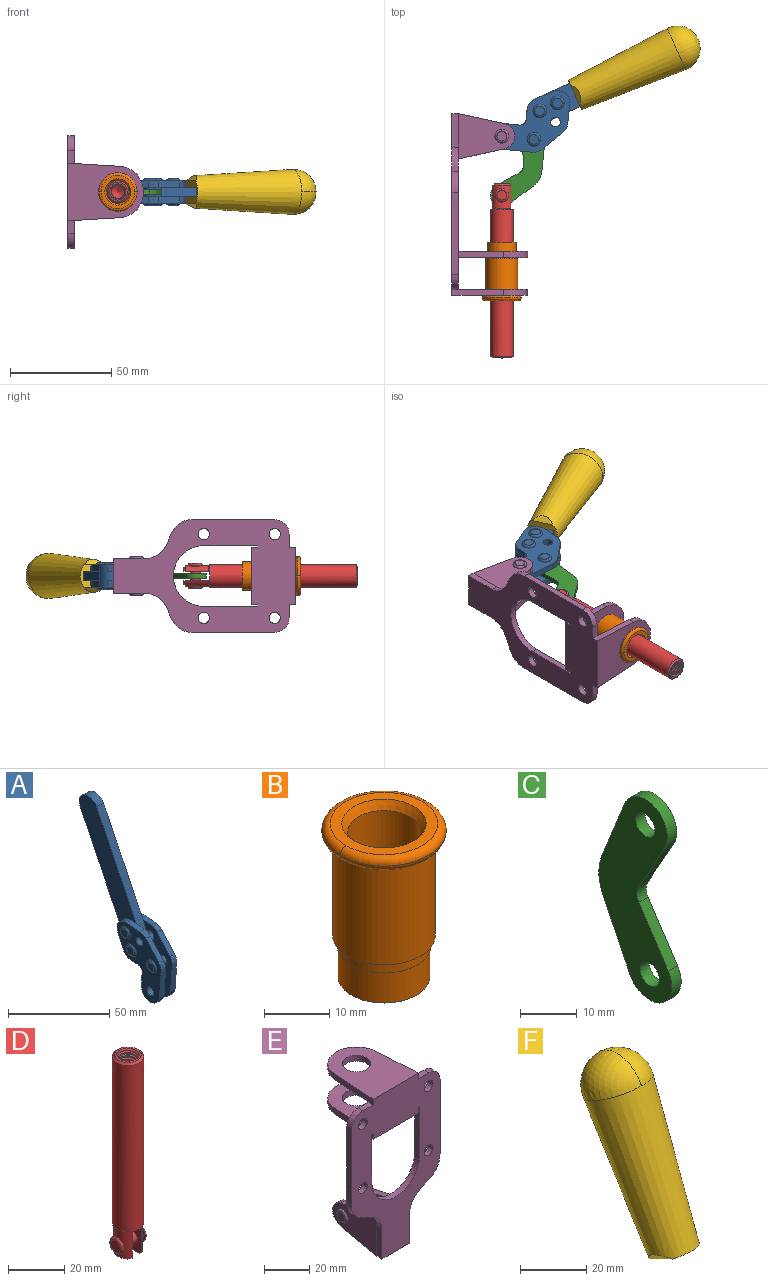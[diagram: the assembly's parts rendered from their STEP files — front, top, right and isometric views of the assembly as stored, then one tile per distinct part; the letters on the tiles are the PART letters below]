
ASSEMBLY  parts=6 mates=6
PART A: 59 faces, bbox 12.9x60.2x99.6 mm
  f0: torus R=2.39mm, axis (-1,0,0), area 14.9mm2, adj f20,f43,f51
  f1: torus R=2.39mm, axis (-1,0,0), area 14.9mm2, adj f19,f42,f51
  f2: torus R=2.39mm, axis (-1,0,0), area 14.9mm2, adj f18,f35,f51
  f3: torus R=2.39mm, axis (-1,0,0), area 14.9mm2, adj f14,f17,f23
  f4: torus R=2.39mm, axis (-1,0,0), area 14.9mm2, adj f13,f16,f23
  f5: torus R=2.39mm, axis (-1,0,0), area 14.9mm2, adj f12,f15,f23
  f6: cylinder r=2.39mm len=4.78mm, axis (1,0,0), area 46.5mm2, adj f48,f50,f51
  f7: cylinder r=2.39mm len=4.78mm, axis (1,0,0), area 46.5mm2, adj f50,f51
  f8: cylinder r=6.35mm len=12.68mm, axis (1,0,0), area 61.8mm2, adj f38,f39,f50,f51
  f9: cylinder r=2.39mm len=4.78mm, axis (-1,0,0), area 70.5mm2, adj f46,f50
  f10: cylinder r=2.39mm len=4.78mm, axis (-1,0,0), area 46.5mm2, adj f23,f45,f46
  f11: cylinder r=2.39mm len=4.78mm, axis (-1,0,0), area 46.5mm2, adj f23,f46
  f12: plane 4.78x4.78mm, normal (1,0,0), area 17.9mm2, adj f5,f15
  f13: plane 4.78x4.78mm, normal (1,0,0), area 17.9mm2, adj f4,f16
  f14: plane 4.78x4.78mm, normal (1,0,0), area 17.9mm2, adj f3,f17
  f15: torus R=2.39mm, axis (-1,0,0), area 14.9mm2, adj f5,f12,f23
  f16: torus R=2.39mm, axis (-1,0,0), area 14.9mm2, adj f4,f13,f23
  f17: torus R=2.39mm, axis (-1,0,0), area 14.9mm2, adj f3,f14,f23
  f18: plane 4.78x4.78mm, normal (-1,0,0), area 17.9mm2, adj f2,f35
  f19: plane 4.78x4.78mm, normal (-1,0,0), area 17.9mm2, adj f1,f42
  f20: plane 4.78x4.78mm, normal (-1,0,0), area 17.9mm2, adj f0,f43
  f21: plane 2.26x0.2mm, normal (1,0,0), area 0.2mm2, adj f31,f44
  f22: plane 2.26x0.2mm, normal (-1,0,0), area 0.2mm2, adj f41,f44
  f23: plane 39.37x30.77mm, normal (1,0,0), area 565.5mm2, adj f3,f4,f5,f10,f11,f15,f16,f17
  f24: cylinder r=6.1mm len=4.15mm, axis (-1,0,0), area 14.7mm2, adj f23,f25,f32,f46
  f25: plane 10.25x9.01mm, normal (0,-0.75,0.66), area 42.3mm2, adj f23,f24,f26,f46
  f26: cylinder r=6.35mm len=4.64mm, axis (-1,0,0), area 15.6mm2, adj f23,f25,f27,f46
  f27: plane 15.84x3.1mm, normal (0,-1,-0.07), area 49.2mm2, adj f23,f26,f28,f46
  f28: cylinder r=6.35mm len=12.68mm, axis (-1,0,0), area 61.8mm2, adj f23,f27,f29,f46
  f29: plane 8.11x3.1mm, normal (0,1,0.07), area 25.2mm2, adj f23,f28,f30,f46
  f30: cylinder r=3.05mm len=3.25mm, axis (-1,0,0), area 14.8mm2, adj f23,f29,f31,f46
  f31: plane 5.99x3.1mm, normal (0,0.07,-1), area 18.6mm2, adj f21,f23,f30,f44,f46
  f32: plane 9.5x3.1mm, normal (0,-0.07,1), area 29.5mm2, adj f23,f24,f33,f46,f47
  f33: cylinder r=6.1mm len=8.63mm, axis (-1,0,0), area 39.1mm2, adj f23,f32,f34,f47
  f34: plane 8.65x3.96mm, normal (0,0.91,-0.42), area 29.5mm2, adj f23,f33,f44,f47
  f35: torus R=2.39mm, axis (-1,0,0), area 14.9mm2, adj f2,f18,f51
  f36: plane 10.25x9.01mm, normal (0,-0.75,0.66), area 42.3mm2, adj f37,f49,f50,f51
  f37: cylinder r=6.35mm len=4.64mm, axis (1,0,0), area 15.6mm2, adj f36,f38,f50,f51
  f38: plane 15.84x3.1mm, normal (0,-1,-0.07), area 49.2mm2, adj f8,f37,f50,f51
  f39: plane 8.11x3.1mm, normal (0,1,0.07), area 25.2mm2, adj f8,f40,f50,f51
  f40: cylinder r=3.05mm len=3.25mm, axis (1,0,0), area 14.8mm2, adj f39,f41,f50,f51
  f41: plane 5.99x3.1mm, normal (0,0.07,-1), area 18.6mm2, adj f22,f40,f44,f50,f51
  f42: torus R=2.39mm, axis (-1,0,0), area 14.9mm2, adj f1,f19,f51
  f43: torus R=2.39mm, axis (-1,0,0), area 14.9mm2, adj f0,f20,f51
  f44: cylinder r=6.35mm len=12.12mm, axis (-1,0,0), area 128.9mm2, adj f21,f22,f23,f31,f34,f41,f46,f47
  f45: plane 2.65x1.35mm, normal (1,0,0), area 1mm2, adj f10,f55
  f46: plane 39.08x20.42mm, normal (-1,0,0), area 412.5mm2, adj f9,f10,f11,f24,f25,f26,f27,f28
  f47: plane 77.62x39.82mm, normal (1,0,0), area 850mm2, adj f32,f33,f34,f44,f53,f54,f55
  f48: plane 2.65x1.35mm, normal (-1,0,0), area 1mm2, adj f6,f55
  f49: cylinder r=6.1mm len=4.15mm, axis (1,0,0), area 14.7mm2, adj f36,f50,f51,f56
  f50: plane 39.08x20.42mm, normal (1,0,0), area 412.5mm2, adj f6,f7,f8,f9,f36,f37,f38,f39
  f51: plane 39.37x30.77mm, normal (-1,0,0), area 565.5mm2, adj f0,f1,f2,f6,f7,f8,f35,f36
  f52: plane 8.65x3.96mm, normal (0,0.91,-0.42), area 29.5mm2, adj f44,f51,f57,f58
  f53: plane 68.49x33.4mm, normal (0,0.9,-0.44), area 358.1mm2, adj f44,f47,f54,f58
  f54: cylinder r=6.35mm len=12.06mm, axis (1,0,0), area 93.7mm2, adj f47,f53,f55,f58
  f55: plane 68.49x33.4mm, normal (0,-0.9,0.44), area 358.1mm2, adj f44,f45,f46,f47,f48,f50,f54,f58
  f56: plane 9.5x3.1mm, normal (0,-0.07,1), area 29.5mm2, adj f49,f50,f51,f57,f58
  f57: cylinder r=6.1mm len=8.63mm, axis (1,0,0), area 39.1mm2, adj f51,f52,f56,f58
  f58: plane 77.62x39.82mm, normal (-1,0,0), area 850mm2, adj f44,f52,f53,f54,f55,f56,f57
PART B: 15 faces, bbox 20.6x20.6x28.7 mm
  f0: torus R=8.26mm, axis (0,0,1), area 56.8mm2, adj f1,f10,f12
  f1: torus R=8.26mm, axis (0,0,1), area 56.8mm2, adj f0,f6,f13
  f2: cylinder r=5.59mm len=25.91mm, axis (0,0,1), area 909.6mm2, adj f3,f4
  f3: cone r=6.86mm half-angle=45deg, axis (0,0,-1), area 70.2mm2, adj f2,f14
  f4: cone r=6.47mm half-angle=30deg, axis (0,0,1), area 66.7mm2, adj f2,f13
  f5: cylinder r=7.04mm len=14.07mm, axis (0,0,1), area 252.6mm2, adj f11,f14
  f6: torus R=8.26mm, axis (0,0,1), area 56.8mm2, adj f1,f12,f13
  f7: cylinder r=7.16mm len=14.33mm, axis (0,0,1), area 91.5mm2, adj f9,f11
  f8: cylinder r=7.86mm len=18.42mm, axis (0,0,1), area 909.6mm2, adj f9,f10
  f9: plane 15.72x15.72mm, normal (0,0,-1), area 33mm2, adj f7,f8
  f10: plane 16.51x16.51mm, normal (0,0,-1), area 19.9mm2, adj f0,f8,f12
  f11: plane 14.33x14.33mm, normal (0,0,-1), area 5.7mm2, adj f5,f7
  f12: torus R=8.26mm, axis (0,0,1), area 56.8mm2, adj f0,f6,f10
  f13: plane 16.51x16.51mm, normal (0,0,1), area 82.7mm2, adj f1,f4,f6
  f14: plane 14.07x14.07mm, normal (0,0,-1), area 7.8mm2, adj f3,f5
PART C: 12 faces, bbox 2.3x18.2x42.8 mm
  f0: cylinder r=2.4mm len=4.8mm, axis (1,0,0), area 34.9mm2, adj f4,f11
  f1: cylinder r=10.41mm len=8.47mm, axis (1,0,0), area 20.2mm2, adj f4,f9,f10,f11
  f2: cylinder r=3.05mm len=3.16mm, axis (1,0,0), area 7.7mm2, adj f4,f6,f7,f11
  f3: cylinder r=2.4mm len=4.8mm, axis (1,0,0), area 34.9mm2, adj f4,f11
  f4: plane 42.81x18.23mm, normal (-1,0,0), area 414.1mm2, adj f0,f1,f2,f3,f5,f6,f7,f8
  f5: cylinder r=5.54mm len=10.67mm, axis (1,0,0), area 41.8mm2, adj f4,f6,f10,f11
  f6: plane 11.66x6.53mm, normal (0,-0.87,-0.49), area 30.9mm2, adj f2,f4,f5,f11
  f7: plane 11.17x7.33mm, normal (0,-0.84,0.55), area 30.9mm2, adj f2,f4,f8,f11
  f8: cylinder r=5.54mm len=10.51mm, axis (1,0,0), area 41.8mm2, adj f4,f7,f9,f11
  f9: plane 13.67x6.67mm, normal (0,0.9,-0.44), area 35.1mm2, adj f1,f4,f8,f11
  f10: plane 14.1x5.7mm, normal (0,0.93,0.37), area 35.1mm2, adj f1,f4,f5,f11
  f11: plane 42.81x18.23mm, normal (1,0,0), area 414.1mm2, adj f0,f1,f2,f3,f5,f6,f7,f8
PART D: 48 faces, bbox 12.6x11.1x86.1 mm
  f0: torus R=2.41mm, axis (-1,0,0), area 15mm2, adj f30,f32,f34
  f1: torus R=2.41mm, axis (-1,0,0), area 15mm2, adj f29,f31,f33
  f2: cylinder r=5.54mm len=72.39mm, axis (0,0,1), area 2518.5mm2, adj f3,f4,f42,f43
  f3: cone r=5.54mm half-angle=45deg, axis (0,0,1), area 7.6mm2, adj f2,f5,f41
  f4: cone r=5.54mm half-angle=45deg, axis (0,0,-1), area 34.9mm2, adj f2,f39
  f5: cylinder r=5.08mm len=11.48mm, axis (0,0,1), area 108.3mm2, adj f3,f7,f8,f41
  f6: cylinder r=2.41mm len=4.83mm, axis (-1,0,0), area 71.2mm2, adj f40,f41
  f7: cylinder r=2.41mm len=4.83mm, axis (-1,0,0), area 7.6mm2, adj f5,f34
  f8: cone r=5.08mm half-angle=45deg, axis (0,0,1), area 10.6mm2, adj f5,f37,f41
  f9: cone r=3.98mm half-angle=45deg, axis (0,0,1), area 17.6mm2, adj f27,f39,f45,f46,f47
  f10: cylinder r=2.41mm len=4.83mm, axis (-1,0,0), area 7.6mm2, adj f33,f38
  f11: cylinder r=3.2mm len=6.4mm, axis (0,0,1), area 78.4mm2, adj f12,f28,f44,f45,f47
  f12: cylinder r=3.2mm len=6.4mm, axis (0,0,1), area 10.5mm2, adj f11,f13,f45,f47
  f13: cylinder r=3.2mm len=6.4mm, axis (0,0,1), area 10.5mm2, adj f12,f14,f45,f47
  f14: cylinder r=3.2mm len=6.4mm, axis (0,0,1), area 10.5mm2, adj f13,f15,f45,f47
  f15: cylinder r=3.2mm len=6.4mm, axis (0,0,1), area 10.5mm2, adj f14,f16,f45,f47
  f16: cylinder r=3.2mm len=6.4mm, axis (0,0,1), area 10.5mm2, adj f15,f17,f45,f47
  f17: cylinder r=3.2mm len=6.4mm, axis (0,0,1), area 10.5mm2, adj f16,f18,f45,f47
  f18: cylinder r=3.2mm len=6.4mm, axis (0,0,1), area 10.5mm2, adj f17,f19,f45,f47
  f19: cylinder r=3.2mm len=6.4mm, axis (0,0,1), area 10.5mm2, adj f18,f20,f45,f47
  f20: cylinder r=3.2mm len=6.4mm, axis (0,0,1), area 10.5mm2, adj f19,f21,f45,f47
  f21: cylinder r=3.2mm len=6.4mm, axis (0,0,1), area 10.5mm2, adj f20,f22,f45,f47
  f22: cylinder r=3.2mm len=6.4mm, axis (0,0,1), area 10.5mm2, adj f21,f23,f45,f47
  f23: cylinder r=3.2mm len=6.4mm, axis (0,0,1), area 10.5mm2, adj f22,f24,f45,f47
  f24: cylinder r=3.2mm len=6.4mm, axis (0,0,1), area 10.5mm2, adj f23,f25,f45,f47
  f25: cylinder r=3.2mm len=6.4mm, axis (0,0,1), area 10.5mm2, adj f24,f26,f45,f47
  f26: cylinder r=3.2mm len=6.4mm, axis (0,0,1), area 10.5mm2, adj f25,f27,f45,f47
  f27: cylinder r=3.2mm len=6.4mm, axis (0,0,1), area 7.4mm2, adj f9,f26,f45,f47
  f28: cone r=3.2mm half-angle=60deg, axis (0,0,1), area 37.2mm2, adj f11
  f29: plane 4.83x4.83mm, normal (-1,0,0), area 18.3mm2, adj f1,f31
  f30: plane 4.83x4.83mm, normal (1,0,0), area 18.3mm2, adj f0,f32
  f31: torus R=2.41mm, axis (-1,0,0), area 15mm2, adj f1,f29,f33
  f32: torus R=2.41mm, axis (-1,0,0), area 15mm2, adj f0,f30,f34
  f33: plane 6.83x6.83mm, normal (1,0,0), area 18.3mm2, adj f1,f10,f31
  f34: plane 6.83x6.83mm, normal (-1,0,0), area 18.3mm2, adj f0,f7,f32
  f35: cone r=5.08mm half-angle=45deg, axis (0,0,1), area 10.6mm2, adj f36,f38,f40
  f36: plane 7.25x1.97mm, normal (0,0,-1), area 10mm2, adj f35,f40
  f37: plane 7.25x1.97mm, normal (0,0,-1), area 10mm2, adj f8,f41
  f38: cylinder r=5.08mm len=11.48mm, axis (0,0,1), area 108.3mm2, adj f10,f35,f40,f42
  f39: plane 9.55x9.55mm, normal (0,0,1), area 22mm2, adj f4,f9
  f40: plane 12.76x10.09mm, normal (1,0,0), area 95.7mm2, adj f6,f35,f36,f38,f42,f43
  f41: plane 12.76x10.09mm, normal (-1,0,0), area 95.7mm2, adj f3,f5,f6,f8,f37,f43
  f42: cone r=5.54mm half-angle=45deg, axis (0,0,1), area 7.6mm2, adj f2,f38,f40
  f43: plane 11.07x4.7mm, normal (0,0,-1), area 50.4mm2, adj f2,f40,f41
  f44: plane 0.89x0.62mm, normal (-1,0,0), area 0.3mm2, adj f11,f45,f46,f47
  f45: bspline ~24.8x7.63mm, area 266.6mm2, adj f9,f11,f12,f13,f14,f15,f16,f17
  f46: bspline ~24.87x7.63mm, area 73.6mm2, adj f9,f44,f45,f47
  f47: bspline ~24.98x7.63mm, area 272.5mm2, adj f9,f11,f12,f13,f14,f15,f16,f17
PART E: 55 faces, bbox 55.7x37.4x89.8 mm
  f0: torus R=2.41mm, axis (-1,0,0), area 15mm2, adj f11,f15,f25
  f1: torus R=2.41mm, axis (-1,0,0), area 15mm2, adj f10,f12,f22
  f2: cylinder r=2.78mm len=5.56mm, axis (0,-1,0), area 54.2mm2, adj f30,f54
  f3: cylinder r=14.99mm len=29.97mm, axis (0,-1,0), area 145.9mm2, adj f30,f49,f53,f54
  f4: cylinder r=2.78mm len=5.56mm, axis (0,-1,0), area 54.2mm2, adj f30,f54
  f5: cylinder r=2.78mm len=5.56mm, axis (0,-1,0), area 54.2mm2, adj f30,f54
  f6: cylinder r=2.78mm len=5.56mm, axis (0,-1,0), area 54.2mm2, adj f30,f54
  f7: cylinder r=6.35mm len=12.7mm, axis (0,0,1), area 123.6mm2, adj f27,f51
  f8: cylinder r=6.35mm len=12.7mm, axis (0,0,-1), area 124.7mm2, adj f21,f35
  f9: cylinder r=2.41mm len=11.18mm, axis (-1,0,0), area 169.4mm2, adj f16,f19
  f10: plane 4.83x4.83mm, normal (1,0,0), area 18.3mm2, adj f1,f12
  f11: plane 4.83x4.83mm, normal (-1,0,0), area 18.3mm2, adj f0,f15
  f12: torus R=2.41mm, axis (-1,0,0), area 15mm2, adj f1,f10,f22
  f13: cylinder r=6.35mm len=12.41mm, axis (1,0,0), area 53.4mm2, adj f18,f19,f22,f23
  f14: cylinder r=6.35mm len=12.41mm, axis (-1,0,0), area 53.4mm2, adj f16,f17,f24,f25
  f15: torus R=2.41mm, axis (-1,0,0), area 15mm2, adj f0,f11,f25
  f16: plane 27.86x22.35mm, normal (1,0,0), area 425.4mm2, adj f9,f14,f17,f24,f30
  f17: plane 22.86x4.97mm, normal (0,0.21,0.98), area 72.5mm2, adj f14,f16,f25,f30
  f18: plane 22.86x4.97mm, normal (0,0.21,0.98), area 72.5mm2, adj f13,f19,f22,f30
  f19: plane 27.86x22.35mm, normal (-1,0,0), area 425.4mm2, adj f9,f13,f18,f23,f30
  f20: cylinder r=12.7mm len=25.35mm, axis (0,0,-1), area 119.8mm2, adj f21,f34,f35,f36
  f21: plane 34.21x28.07mm, normal (0,0,-1), area 702.4mm2, adj f8,f20,f30,f34,f36
  f22: plane 27.96x22.45mm, normal (1,0,0), area 407.2mm2, adj f1,f12,f13,f18,f23,f30,f42,f43
  f23: plane 22.86x4.97mm, normal (0,0.21,-0.98), area 72.5mm2, adj f13,f19,f22,f44
  f24: plane 22.86x4.97mm, normal (0,0.21,-0.98), area 72.5mm2, adj f14,f16,f25,f44
  f25: plane 27.86x22.35mm, normal (-1,0,0), area 407.1mm2, adj f0,f14,f15,f17,f24,f30,f45,f46
  f26: plane 3.1x0.95mm, normal (0,0,-1), area 2.7mm2, adj f30,f49,f50,f54
  f27: plane 34.21x28.07mm, normal (0,0,1), area 702.4mm2, adj f7,f28,f30,f50,f52
  f28: cylinder r=12.7mm len=25.35mm, axis (0,0,1), area 118.8mm2, adj f27,f50,f51,f52
  f29: plane 3.1x0.95mm, normal (0,0,-1), area 2.7mm2, adj f30,f52,f53,f54
  f30: plane 86.54x55.63mm, normal (0,1,0), area 2362.9mm2, adj f2,f3,f4,f5,f6,f16,f17,f18
  f31: plane 40.56x3.1mm, normal (-1,0,0), area 125.7mm2, adj f30,f32,f48,f54
  f32: cylinder r=7.11mm len=7.11mm, axis (0,-1,0), area 34.6mm2, adj f30,f31,f33,f54
  f33: plane 6.67x3.1mm, normal (0,0,1), area 20.4mm2, adj f30,f32,f34,f54
  f34: plane 25.39x3.13mm, normal (-1,0.06,0), area 79.5mm2, adj f20,f21,f33,f35,f54
  f35: plane 37.31x28.45mm, normal (0,0,1), area 789.9mm2, adj f8,f20,f34,f36,f54
  f36: plane 25.39x3.13mm, normal (1,0.06,0), area 79.5mm2, adj f20,f21,f35,f37,f54
  f37: plane 6.67x3.1mm, normal (0,0,1), area 20.4mm2, adj f30,f36,f38,f54
  f38: cylinder r=7.11mm len=7.11mm, axis (0,-1,0), area 34.6mm2, adj f30,f37,f39,f54
  f39: plane 40.56x3.1mm, normal (1,0,0), area 125.7mm2, adj f30,f38,f40,f54
  f40: cylinder r=11.18mm len=10.16mm, axis (0,-1,0), area 39.5mm2, adj f30,f39,f41,f54
  f41: plane 6.09x3.1mm, normal (0.42,0,-0.91), area 20.8mm2, adj f30,f40,f42,f54
  f42: cylinder r=11.18mm len=9.41mm, axis (0,-1,0), area 37.2mm2, adj f22,f30,f41,f43,f54
  f43: plane 16.5x3.1mm, normal (1,0,0), area 51.1mm2, adj f22,f42,f44,f54
  f44: plane 17.37x3.1mm, normal (0,0,-1), area 53.8mm2, adj f23,f24,f30,f43,f45,f54
  f45: plane 16.5x3.1mm, normal (-1,0,0), area 51.1mm2, adj f25,f44,f46,f54
  f46: cylinder r=11.18mm len=9.41mm, axis (0,-1,0), area 37.2mm2, adj f25,f30,f45,f47,f54
  f47: plane 6.09x3.1mm, normal (-0.42,0,-0.91), area 20.8mm2, adj f30,f46,f48,f54
  f48: cylinder r=11.18mm len=10.16mm, axis (0,-1,0), area 39.5mm2, adj f30,f31,f47,f54
  f49: plane 26.54x3.1mm, normal (-1,0,0), area 82.3mm2, adj f3,f26,f30,f54
  f50: plane 25.39x3.1mm, normal (1,0.06,0), area 78.8mm2, adj f26,f27,f28,f51,f54
  f51: plane 37.31x28.45mm, normal (0,0,-1), area 789.9mm2, adj f7,f28,f50,f52,f54
  f52: plane 25.39x3.1mm, normal (-1,0.06,0), area 78.8mm2, adj f27,f28,f29,f51,f54
  f53: plane 26.54x3.1mm, normal (1,0,0), area 82.3mm2, adj f3,f29,f30,f54
  f54: plane 89.66x55.63mm, normal (0,-1,0), area 2678.5mm2, adj f2,f3,f4,f5,f6,f26,f29,f31
PART F: 11 faces, bbox 22.3x42.6x64.5 mm
  f0: sphere r=11.13mm, area 411.4mm2, adj f1,f8
  f1: cone r=11.11mm half-angle=3.3deg, axis (0,0.44,0.9), area 3251.8mm2, adj f0,f7,f8,f9,f10
  f2: cylinder r=6.16mm len=11.7mm, axis (1,0,0), area 89.5mm2, adj f3,f4,f5,f6
  f3: plane 60.23x36.75mm, normal (-1,0,0), area 763.6mm2, adj f2,f4,f6,f10
  f4: plane 51.37x25.05mm, normal (0,0.9,-0.44), area 264.2mm2, adj f2,f3,f5,f10
  f5: plane 60.23x36.75mm, normal (1,0,0), area 763.6mm2, adj f2,f4,f6,f10
  f6: plane 51.37x25.05mm, normal (0,-0.9,0.44), area 264.2mm2, adj f2,f3,f5,f10
  f7: plane 9.95x5.95mm, normal (0.71,-0.31,-0.64), area 25.8mm2, adj f1,f10
  f8: sphere r=11.13mm, area 411.4mm2, adj f0,f1
  f9: plane 9.95x5.95mm, normal (-0.71,-0.31,-0.64), area 25.8mm2, adj f1,f10
  f10: plane 14.27x11.38mm, normal (0,-0.44,-0.9), area 106.7mm2, adj f1,f3,f4,f5,f6,f7,f9
PLACE A rot(axis=(0.01,1,-0.01),90deg) t=(37.34,8.14,0)mm
PLACE B rot(axis=(0,-0.71,0.71),180deg) t=(5.96,1.56,24.61)mm
PLACE C rot(axis=(0.66,0.37,-0.66),139.8deg) t=(-6.79,30.69,0)mm
PLACE D rot(axis=(0.58,0.58,-0.58),120deg) t=(-18.66,20.03,0)mm
PLACE E rot(axis=(0.58,0.58,-0.58),120deg) t=(-18.66,1.56,0)mm fixed
PLACE F rot(axis=(0.01,1,-0.01),90deg) t=(37.34,8.14,0.04)mm
MATE slider D.f2 <-> B.f2  axis (0,-1,0) through (5.96,-38.75,0)mm
MATE fastened A.f54 <-> F.f2  axis (0,0,1) through (94.11,77.6,2.35)mm
MATE revolute A.f7 <-> E.f0  axis (0,0,1) through (5.96,33.65,0)mm
MATE fastened B.f2 <-> E.f7  axis (0,1,0) through (5.96,-44.83,0)mm
MATE revolute C.f3 <-> A.f4  axis (0,0,-1) through (21.75,32.1,0)mm
MATE revolute C.f5 <-> D.f6  axis (0,0,-1) through (5.96,4.56,0)mm
